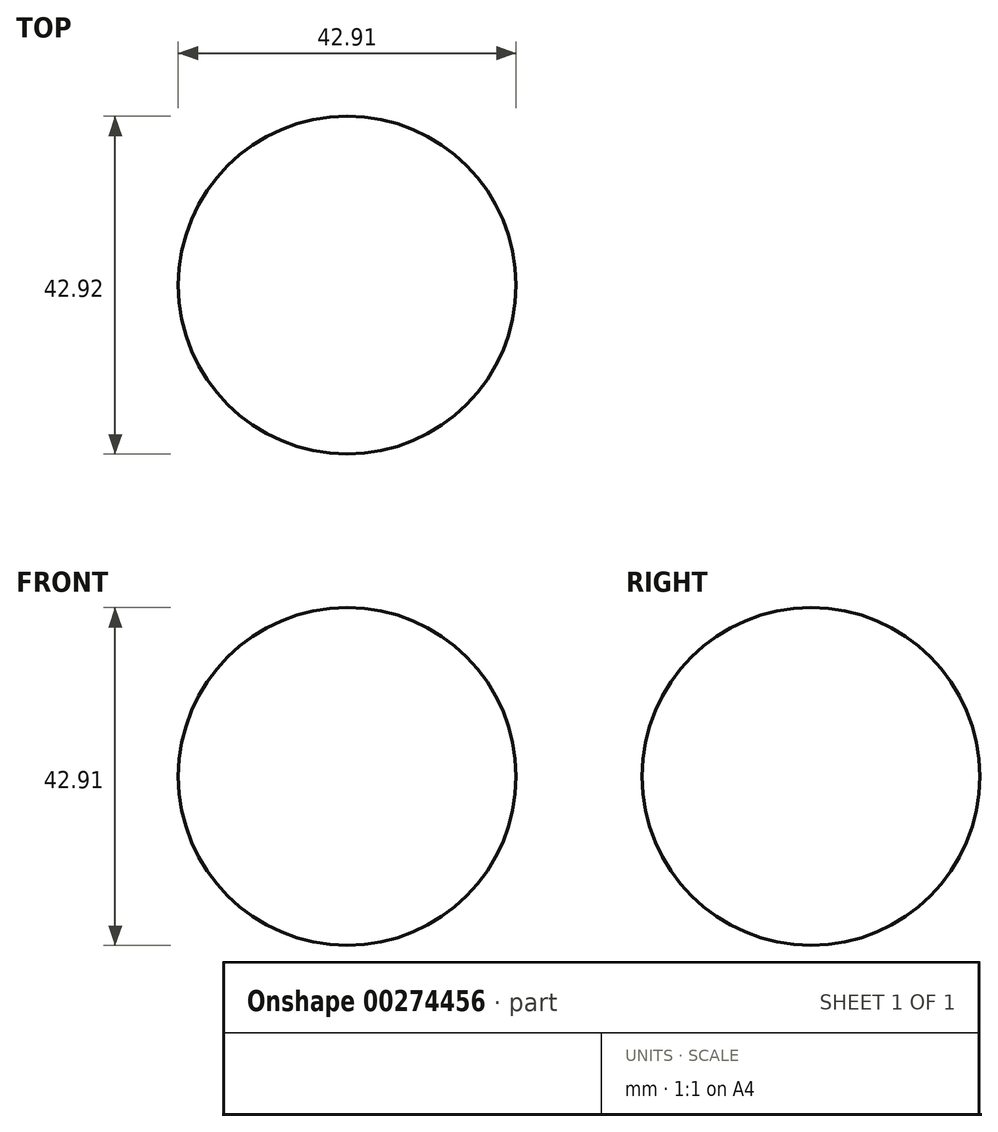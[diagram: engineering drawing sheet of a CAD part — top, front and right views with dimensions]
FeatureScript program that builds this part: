
annotation { "Feature Type Name" : "Feature", "Feature Type Description" : "" }
export const myFeature = defineFeature(function(context is Context, id is Id, definition is map)
    precondition{}
    {
        {
            var Q0;
            Q0=qCreatedBy(makeId("Front.planeOp"),FACE);
            var sketch = newSketch(context, id + "F0", { "sketchPlane" : qUnion([Q0])});
            skArc(sketch, "E0", {"start": v(-36.66, 48.57) * mm, "mid": v(-58.12, 27.12) * mm, "end": v(-36.66, 5.66) * mm});
            skLineSegment(sketch, "E1", {"start": v(-36.66, 48.57) * mm, "end": v(-36.66, 5.66) * mm});
            skSolve(sketch);
        }
        {
            var Q0;
            Q0 = qSketchRegion(id + "F0", true);
            var Q1;
            Q1=sQuery(id+"F0.wireOp",EDGE,"E1");
            revolve(context, id + "F1", {"entities" : qUnion([Q0]), "axis" : qUnion([Q1]), "revolveType" : RevolveType.FULL});
        }
    });
